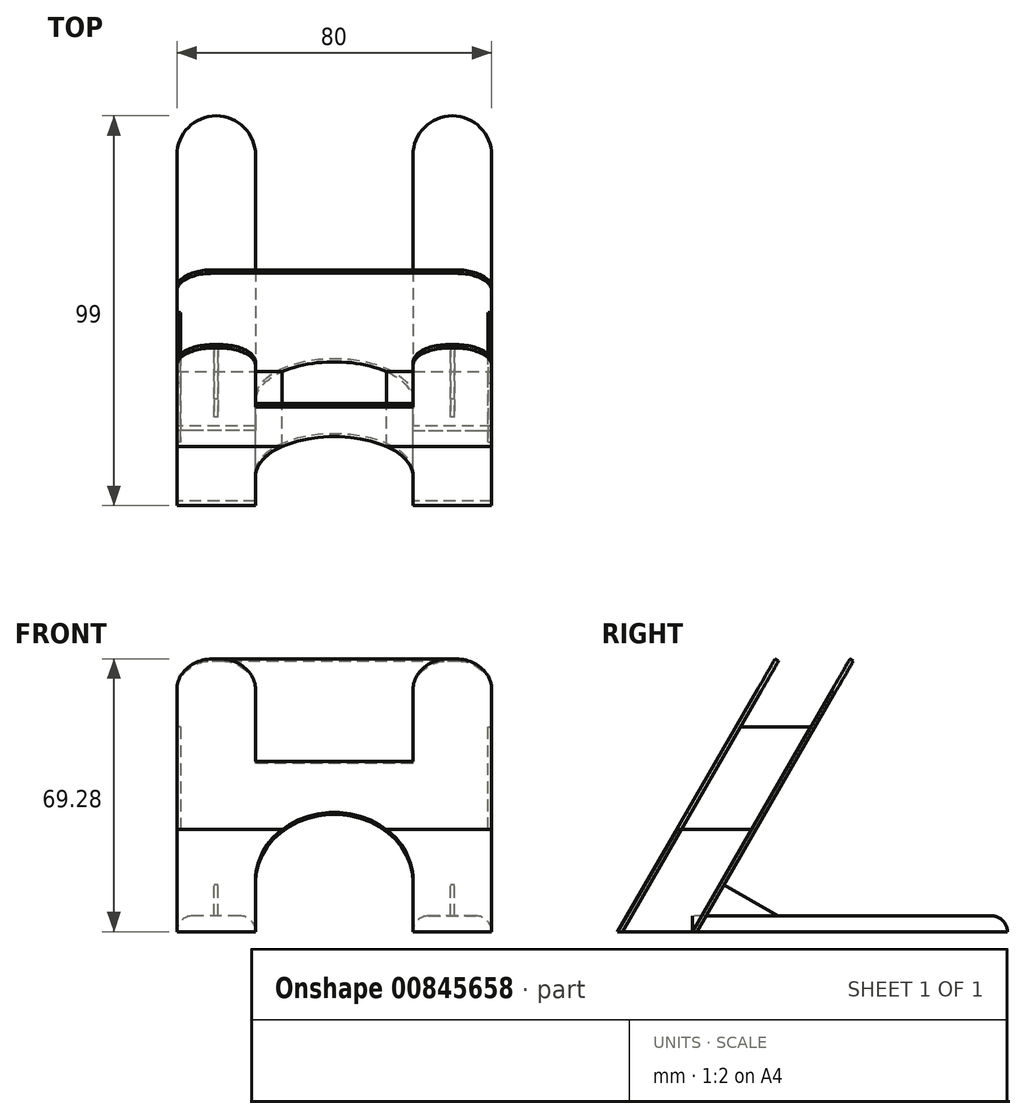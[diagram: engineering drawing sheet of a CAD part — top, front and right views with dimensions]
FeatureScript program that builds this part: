
annotation { "Feature Type Name" : "Feature", "Feature Type Description" : "" }
export const myFeature = defineFeature(function(context is Context, id is Id, definition is map)
    precondition{}
    {
        {
            var Q0;
            Q0=qCreatedBy(makeId("Top.planeOp"),FACE);
            var sketch = newSketch(context, id + "F0", { "sketchPlane" : qUnion([Q0])});
            skLineSegment(sketch, "E0.bottom", {"start": v(-30, 49.5) * mm, "end": v(-30, 49.5) * mm});
            skLineSegment(sketch, "E0.top", {"start": v(-40, -49.5) * mm, "end": v(40, -49.5) * mm});
            skLineSegment(sketch, "E0.left", {"start": v(-40, 39.5) * mm, "end": v(-40, -49.5) * mm});
            skLineSegment(sketch, "E0.right", {"start": v(40, 39.5) * mm, "end": v(40, -49.5) * mm});
            skPoint(sketch, "E0.middle", {"position": v(0, 0) * mm});
            skLineSegment(sketch, "E1.bottom", {"start": v(-20, 49.5) * mm, "end": v(-20, 49.5) * mm});
            skLineSegment(sketch, "E1.top", {"start": v(-20, -30.5) * mm, "end": v(20, -30.5) * mm});
            skLineSegment(sketch, "E1.left", {"start": v(-20, 39.5) * mm, "end": v(-20, -30.5) * mm});
            skLineSegment(sketch, "E1.right", {"start": v(20, 49.5) * mm, "end": v(20, 40) * mm});
            skLineSegment(sketch, "E2.bottom", {"start": v(20, -30.5) * mm, "end": v(-20, -30.5) * mm});
            skLineSegment(sketch, "E2.top", {"start": v(20, -49.5) * mm, "end": v(-20, -49.5) * mm});
            skLineSegment(sketch, "E2.left", {"start": v(20, -30.5) * mm, "end": v(20, -49.5) * mm});
            skLineSegment(sketch, "E2.right", {"start": v(-20, -30.5) * mm, "end": v(-20, -49.5) * mm});
            skLineSegment(sketch, "E3", {"start": v(-20, -30.5) * mm, "end": v(-40, -30.5) * mm});
            skLineSegment(sketch, "E4", {"start": v(20, -30.5) * mm, "end": v(40, -30.5) * mm});
            skLineSegment(sketch, "E5", {"start": v(20, 39.5) * mm, "end": v(20, -30.5) * mm});
            skLineSegment(sketch, "E6.trimOffspring", {"start": v(30, 49.5) * mm, "end": v(30, 49.5) * mm});
            skLineSegment(sketch, "E7", {"start": v(0, 54.54) * mm, "end": v(0, -63.88) * mm, "construction": true});
            skPoint(sketch, "E8.visualSharp", {"position": v(-40, 49.5) * mm});
            skArc(sketch, "E8.filletArc", {"start": v(-30, 49.5) * mm, "mid": v(-37.07, 46.57) * mm, "end": v(-40, 39.5) * mm});
            skPoint(sketch, "E9.visualSharp", {"position": v(-20, 49.5) * mm});
            skArc(sketch, "E9.filletArc", {"start": v(-20, 39.5) * mm, "mid": v(-22.93, 46.57) * mm, "end": v(-30, 49.5) * mm});
            skPoint(sketch, "E10.visualSharp", {"position": v(20, 49.5) * mm});
            skArc(sketch, "E10.filletArc", {"start": v(30, 49.5) * mm, "mid": v(22.93, 46.57) * mm, "end": v(20, 39.5) * mm});
            skPoint(sketch, "E11.visualSharp", {"position": v(40, 49.5) * mm});
            skArc(sketch, "E11.filletArc", {"start": v(40, 39.5) * mm, "mid": v(37.07, 46.57) * mm, "end": v(30, 49.5) * mm});
            skLineSegment(sketch, "E12", {"start": v(30, 49.5) * mm, "end": v(30, -55.74) * mm, "construction": true});
            skLineSegment(sketch, "E13", {"start": v(-30, 49.5) * mm, "end": v(-30, -57.66) * mm, "construction": true});
            skSolve(sketch);
        }
        {
            var Q0;
            Q0=sQuery(id+"F0.wireOp",EDGE,"E0.top");
            cPlane(context, id + "F1", {"entities" : qUnion([Q0]), "cplaneType" : CPlaneType.LINE_ANGLE, "offset" : 25 * mm, "angle" : 30 * degree, "oppositeDirection" : true, "width" : 150 * mm, "height" : 150 * mm});
        }
        {
            var Q0;
            Q0=sQuery(id+"F0.wireOp",EDGE,"E1.top");
            cPlane(context, id + "F2", {"entities" : qUnion([Q0]), "cplaneType" : CPlaneType.LINE_ANGLE, "offset" : 20 * mm, "angle" : 30 * degree, "oppositeDirection" : true, "width" : 150 * mm, "height" : 150 * mm});
        }
        {
            var Q0;
            Q0=qCreatedBy(id+"F2.planeOp",FACE);
            var sketch = newSketch(context, id + "F3", { "sketchPlane" : qUnion([Q0])});
            skLineSegment(sketch, "E14.bottom", {"start": v(40, -15.25) * mm, "end": v(-40, -15.25) * mm});
            skLineSegment(sketch, "E14.left", {"start": v(40, -15.25) * mm, "end": v(40, 64.75) * mm});
            skLineSegment(sketch, "E14.right", {"start": v(-40, -15.25) * mm, "end": v(-40, 64.75) * mm});
            skLineSegment(sketch, "E15.bottom", {"start": v(-20, -15.25) * mm, "end": v(20, -15.25) * mm});
            skLineSegment(sketch, "E15.top", {"start": v(0, 19.75) * mm, "end": v(0, 19.75) * mm});
            skLineSegment(sketch, "E15.left", {"start": v(-20, -15.25) * mm, "end": v(-20, -0.25) * mm});
            skLineSegment(sketch, "E15.right", {"start": v(20, -15.25) * mm, "end": v(20, -0.25) * mm});
            skPoint(sketch, "E16.visualSharp", {"position": v(-20, 19.75) * mm});
            skArc(sketch, "E16.filletArc", {"start": v(0, 19.75) * mm, "mid": v(-14.14, 13.9) * mm, "end": v(-20, -0.25) * mm});
            skPoint(sketch, "E17.visualSharp", {"position": v(20, 19.75) * mm});
            skArc(sketch, "E17.filletArc", {"start": v(20, -0.25) * mm, "mid": v(14.14, 13.9) * mm, "end": v(0, 19.75) * mm});
            skLineSegment(sketch, "E18", {"start": v(40, 14.75) * mm, "end": v(13.23, 14.75) * mm});
            skLineSegment(sketch, "E19", {"start": v(-13.23, 14.75) * mm, "end": v(-40, 14.75) * mm});
            skLineSegment(sketch, "E20", {"start": v(0, 99.97) * mm, "end": v(0, -38.35) * mm, "construction": true});
            skLineSegment(sketch, "E21.trimOffspring", {"start": v(40, 64.75) * mm, "end": v(-40, 64.75) * mm});
            skSolve(sketch);
        }
        {
            var Q0;
            Q0=qCreatedBy(id+"F1.planeOp",FACE);
            var sketch = newSketch(context, id + "F4", { "sketchPlane" : qUnion([Q0])});
            skLineSegment(sketch, "E22.bottom", {"start": v(40, -24.75) * mm, "end": v(-40, -24.75) * mm});
            skLineSegment(sketch, "E22.top", {"start": v(40, 55.25) * mm, "end": v(20, 55.25) * mm});
            skLineSegment(sketch, "E22.left", {"start": v(40, -24.75) * mm, "end": v(40, 55.25) * mm});
            skLineSegment(sketch, "E22.right", {"start": v(-40, -24.75) * mm, "end": v(-40, 55.25) * mm});
            skLineSegment(sketch, "E23.top", {"start": v(-20, 25.25) * mm, "end": v(20, 25.25) * mm});
            skLineSegment(sketch, "E23.left", {"start": v(-20, 55.25) * mm, "end": v(-20, 25.25) * mm});
            skLineSegment(sketch, "E23.right", {"start": v(20, 55.38) * mm, "end": v(20, 25.25) * mm});
            skLineSegment(sketch, "E24.bottom", {"start": v(-20, -24.75) * mm, "end": v(20, -24.75) * mm});
            skLineSegment(sketch, "E24.top", {"start": v(0, 10.25) * mm, "end": v(0, 10.25) * mm});
            skLineSegment(sketch, "E24.left", {"start": v(-20, -24.75) * mm, "end": v(-20, -9.75) * mm});
            skLineSegment(sketch, "E24.right", {"start": v(20, -24.75) * mm, "end": v(20, -9.75) * mm});
            skPoint(sketch, "E25.visualSharp", {"position": v(-20, 10.25) * mm});
            skArc(sketch, "E25.filletArc", {"start": v(0, 10.25) * mm, "mid": v(-14.14, 4.4) * mm, "end": v(-20, -9.75) * mm});
            skPoint(sketch, "E26.visualSharp", {"position": v(20, 10.25) * mm});
            skArc(sketch, "E26.filletArc", {"start": v(20, -9.75) * mm, "mid": v(14.14, 4.4) * mm, "end": v(0, 10.25) * mm});
            skLineSegment(sketch, "E27", {"start": v(40, 5.25) * mm, "end": v(13.23, 5.25) * mm});
            skLineSegment(sketch, "E28", {"start": v(-13.23, 5.25) * mm, "end": v(-40, 5.25) * mm});
            skLineSegment(sketch, "E29", {"start": v(0, 87.55) * mm, "end": v(0, -88.72) * mm, "construction": true});
            skLineSegment(sketch, "E30", {"start": v(20, 55.38) * mm, "end": v(20, 55.38) * mm});
            skLineSegment(sketch, "E31", {"start": v(-20, 55.25) * mm, "end": v(-40, 55.25) * mm});
            skSolve(sketch);
        }
        {
            var Q0;
            {var subQ2=sQuery(id+"F0.wireOp",EDGE,"E4");Q0=makeQuery(id+"F0.imprint","IMPRINT",FACE,{"disambiguationData":[TD([[makeQuery(id+"F0.imprint","IMPRINT",EDGE,{"derivedFrom":subQ2}),1.0]])]});}
            var Q1;
            Q1=makeQuery(id+"F0.imprint","IMPRINT",FACE,{"disambiguationData":[TD([[makeQuery(id+"F0.imprint","IMPRINT",EDGE,{"derivedFrom":sQuery(id+"F0.wireOp",EDGE,"E1.left")}),-1.0]])]});
            extrude(context, id + "F5", {"entities" : qUnion([Q0, Q1]), "depth" : 4 * mm, "offsetDistance" : 25 * mm});
        }
        {
            var Q0;
            {var subQ1=sQuery(id+"F4.wireOp",EDGE,"E24.left");Q0=makeQuery(id+"F4.imprint","IMPRINT",FACE,{"disambiguationData":[TD([[makeQuery(id+"F4.imprint","IMPRINT",EDGE,{"derivedFrom":subQ1}),1.0]])]});}
            var Q1;
            {var subQ6=sQuery(id+"F4.wireOp",EDGE,"E22.top");Q1=makeQuery(id+"F4.imprint","IMPRINT",FACE,{"disambiguationData":[TD([[makeQuery(id+"F4.imprint","IMPRINT",EDGE,{"derivedFrom":subQ6}),1.0]])]});}
            var Q2;
            {var subQ1=sQuery(id+"F4.wireOp",EDGE,"E24.right");Q2=makeQuery(id+"F4.imprint","IMPRINT",FACE,{"disambiguationData":[TD([[makeQuery(id+"F4.imprint","IMPRINT",EDGE,{"derivedFrom":subQ1}),-1.0]])]});}
            extrude(context, id + "F6", {"entities" : qUnion([Q0, Q1, Q2]), "depth" : 1 * mm, "offsetDistance" : 25 * mm});
        }
        {
            var Q0;
            {var subQ1=sQuery(id+"F3.wireOp",EDGE,"E15.left");Q0=makeQuery(id+"F3.imprint","IMPRINT",FACE,{"disambiguationData":[TD([[makeQuery(id+"F3.imprint","IMPRINT",EDGE,{"derivedFrom":subQ1}),1.0]])]});}
            var Q1;
            {var subQ5=sQuery(id+"F3.wireOp",EDGE,"E14.top");Q1=makeQuery(id+"F3.imprint","IMPRINT",FACE,{"disambiguationData":[TD([[makeQuery(id+"F3.imprint","IMPRINT",EDGE,{"derivedFrom":subQ5}),1.0]])]});}
            var Q2;
            {var subQ1=sQuery(id+"F3.wireOp",EDGE,"E15.right");Q2=makeQuery(id+"F3.imprint","IMPRINT",FACE,{"disambiguationData":[TD([[makeQuery(id+"F3.imprint","IMPRINT",EDGE,{"derivedFrom":subQ1}),-1.0]])]});}
            var Q3;
            {var subQ3=sQuery(id+"F3.wireOp",EDGE,"E18");Q3=makeQuery(id+"F3.imprint","IMPRINT",FACE,{"disambiguationData":[TD([[makeQuery(id+"F3.imprint","IMPRINT",EDGE,{"derivedFrom":subQ3}),-1.0]])]});}
            extrude(context, id + "F7", {"entities" : qUnion([Q0, Q1, Q2, Q3]), "depth" : 1 * mm, "offsetDistance" : 25 * mm});
        }
        {
            var Q0;
            {var subQ1=sQuery(id+"F4.wireOp",EDGE,"E24.left");Q0=makeQuery(id+"F4.imprint","IMPRINT",FACE,{"disambiguationData":[TD([[makeQuery(id+"F4.imprint","IMPRINT",EDGE,{"derivedFrom":subQ1}),1.0]])]});}
            var Q1;
            {var subQ1=sQuery(id+"F3.wireOp",EDGE,"E15.left");Q1=makeQuery(id+"F3.imprint","IMPRINT",FACE,{"disambiguationData":[TD([[makeQuery(id+"F3.imprint","IMPRINT",EDGE,{"derivedFrom":subQ1}),1.0]])]});}
            loft(context, id + "F8", {"sheetProfilesArray" : [{ "sheetProfileEntities" : qUnion([Q0]) }, { "sheetProfileEntities" : qUnion([Q1]) }]});
        }
        {
            var Q0;
            {var subQ1=sQuery(id+"F4.wireOp",EDGE,"E24.right");Q0=makeQuery(id+"F4.imprint","IMPRINT",FACE,{"disambiguationData":[TD([[makeQuery(id+"F4.imprint","IMPRINT",EDGE,{"derivedFrom":subQ1}),-1.0]])]});}
            var Q1;
            {var subQ1=sQuery(id+"F3.wireOp",EDGE,"E15.right");Q1=makeQuery(id+"F3.imprint","IMPRINT",FACE,{"disambiguationData":[TD([[makeQuery(id+"F3.imprint","IMPRINT",EDGE,{"derivedFrom":subQ1}),-1.0]])]});}
            loft(context, id + "F9", {"sheetProfilesArray" : [{ "sheetProfileEntities" : qUnion([Q0]) }, { "sheetProfileEntities" : qUnion([Q1]) }]});
        }
        {
            var Q0;
            Q0=makeQuery(id+"F6.opExtrude","SWEPT_EDGE",EDGE,{"disambiguationData":[OSD([sQuery(id+"F4.wireOp",EDGE,"E22.top"),sQuery(id+"F4.wireOp",EDGE,"E22.left")])]});
            var Q1;
            Q1=makeQuery(id+"F6.opExtrude","SWEPT_EDGE",EDGE,{"disambiguationData":[OSD([sQuery(id+"F4.wireOp",EDGE,"E22.top"),sQuery(id+"F4.wireOp",EDGE,"E23.right")])]});
            var Q2;
            Q2=makeQuery(id+"F7.opExtrude","SWEPT_EDGE",EDGE,{"disambiguationData":[OSD([sQuery(id+"F3.wireOp",EDGE,"E14.top"),sQuery(id+"F3.wireOp",EDGE,"af3756bd-d7f4-4d2d-9217-8fff7642af17.right")])]});
            var Q3;
            {var subQ0=sQuery(id+"F3.wireOp",EDGE,"E21.trimOffspring");Q3=qUnion([makeQuery(id+"F7.opExtrude","SWEPT_EDGE",EDGE,{"disambiguationData":[OSD([sQuery(id+"F3.wireOp",EDGE,"E14.right"),subQ0])]}),makeQuery(id+"F7.opExtrude","SWEPT_EDGE",EDGE,{"disambiguationData":[OSD([sQuery(id+"F3.wireOp",EDGE,"E14.left"),subQ0])]})]);}
            var Q4;
            Q4=makeQuery(id+"F7.opExtrude","SWEPT_EDGE",EDGE,{"disambiguationData":[OSD([sQuery(id+"F3.wireOp",EDGE,"E14.right"),sQuery(id+"F3.wireOp",EDGE,"E21.trimOffspring")])]});
            var Q5;
            Q5=makeQuery(id+"F6.opExtrude","SWEPT_EDGE",EDGE,{"disambiguationData":[OSD([sQuery(id+"F4.wireOp",EDGE,"E22.right"),sQuery(id+"F4.wireOp",EDGE,"E31")])]});
            var Q6;
            Q6=makeQuery(id+"F6.opExtrude","SWEPT_EDGE",EDGE,{"disambiguationData":[OSD([sQuery(id+"F4.wireOp",EDGE,"E23.left"),sQuery(id+"F4.wireOp",EDGE,"E31")])]});
            fillet(context, id + "F10", {"entities" : qUnion([Q0, Q1, Q2, Q3, Q4, Q5, Q6]), "radius" : 9 * mm, "tangentPropagation" : true, "allowEdgeOverflow" : false});
        }
        {
            var Q0;
            Q0=makeQuery(id+"F5.opExtrude","CAP_EDGE",EDGE,{"disambiguationData":[OSD([sQuery(id+"F0.wireOp",EDGE,"E0.left")])],"isStart":false});
            var Q1;
            Q1=makeQuery(id+"F5.opExtrude","CAP_EDGE",EDGE,{"disambiguationData":[OSD([sQuery(id+"F0.wireOp",EDGE,"E1.left")])],"isStart":false});
            var Q2;
            Q2=makeQuery(id+"F5.opExtrude","CAP_EDGE",EDGE,{"disambiguationData":[OSD([sQuery(id+"F0.wireOp",EDGE,"E5")])],"isStart":false});
            var Q3;
            Q3=makeQuery(id+"F5.opExtrude","CAP_EDGE",EDGE,{"disambiguationData":[OSD([sQuery(id+"F0.wireOp",EDGE,"E0.right")])],"isStart":false});
            var Q4;
            Q4=makeQuery(id+"F5.opExtrude","CAP_EDGE",EDGE,{"disambiguationData":[OSD([sQuery(id+"F0.wireOp",EDGE,"E10.filletArc"),sQuery(id+"F0.wireOp",EDGE,"E11.filletArc")])],"isStart":false});
            var Q5;
            Q5=makeQuery(id+"F5.opExtrude","CAP_EDGE",EDGE,{"disambiguationData":[OSD([sQuery(id+"F0.wireOp",EDGE,"E8.filletArc"),sQuery(id+"F0.wireOp",EDGE,"E9.filletArc")])],"isStart":false});
            fillet(context, id + "F11", {"entities" : qUnion([Q0, Q1, Q2, Q3, Q4, Q5]), "radius" : 4 * mm, "tangentPropagation" : true, "allowEdgeOverflow" : false});
        }
        {
            var Q0;
            Q0=makeQuery(id+"F9.opLoft","SWEPT_FACE",FACE,{"disambiguationData":[OSD([sQuery(id+"F3.wireOp",EDGE,"E14.bottom"),sQuery(id+"F3.wireOp",EDGE,"E14.left"),sQuery(id+"F3.wireOp",EDGE,"E18"),sQuery(id+"F4.wireOp",EDGE,"E22.bottom"),sQuery(id+"F4.wireOp",EDGE,"E22.left"),sQuery(id+"F4.wireOp",EDGE,"E27")])]});
            cPlane(context, id + "F12", {"entities" : qUnion([Q0]), "cplaneType" : CPlaneType.OFFSET, "offset" : 0 * mm, "width" : 150 * mm, "height" : 150 * mm});
        }
        {
            var Q0;
            Q0=makeQuery(id+"F8.opLoft","SWEPT_FACE",FACE,{"disambiguationData":[OSD([sQuery(id+"F3.wireOp",EDGE,"E14.bottom"),sQuery(id+"F3.wireOp",EDGE,"E14.right"),sQuery(id+"F3.wireOp",EDGE,"E19"),sQuery(id+"F4.wireOp",EDGE,"E22.bottom"),sQuery(id+"F4.wireOp",EDGE,"E22.right"),sQuery(id+"F4.wireOp",EDGE,"E28")])]});
            cPlane(context, id + "F13", {"entities" : qUnion([Q0]), "cplaneType" : CPlaneType.OFFSET, "offset" : 0 * mm, "width" : 150 * mm, "height" : 150 * mm});
        }
        {
            var Q0;
            Q0=qCreatedBy(id+"F12.planeOp",FACE);
            var sketch = newSketch(context, id + "F14", { "sketchPlane" : qUnion([Q0])});
            skLineSegment(sketch, "E32", {"start": v(33.35, 25.98) * mm, "end": v(15.5, 25.98) * mm});
            skLineSegment(sketch, "E33", {"start": v(15.5, 25.98) * mm, "end": v(0.5, 51.96) * mm});
            skLineSegment(sketch, "E34", {"start": v(0.5, 51.96) * mm, "end": v(18.35, 51.96) * mm});
            skLineSegment(sketch, "E35", {"start": v(18.35, 51.96) * mm, "end": v(33.35, 25.98) * mm});
            skSolve(sketch);
        }
        {
            var Q0;
            Q0=makeQuery(id+"F14.imprint","IMPRINT",FACE,{"disambiguationData":[TD([[makeQuery(id+"F14.imprint","IMPRINT",EDGE,{"derivedFrom":sQuery(id+"F14.wireOp",EDGE,"E32")}),-1.0]])]});
            extrude(context, id + "F15", {"entities" : qUnion([Q0]), "oppositeDirection" : true, "depth" : 1 * mm, "offsetDistance" : 25 * mm});
        }
        {
            var Q0;
            Q0=qCreatedBy(id+"F13.planeOp",FACE);
            var sketch = newSketch(context, id + "F16", { "sketchPlane" : qUnion([Q0])});
            skLineSegment(sketch, "E36", {"start": v(-33.35, 25.98) * mm, "end": v(-18.35, 51.96) * mm});
            skLineSegment(sketch, "E37", {"start": v(-18.35, 51.96) * mm, "end": v(-0.5, 51.96) * mm});
            skLineSegment(sketch, "E38", {"start": v(-0.5, 51.96) * mm, "end": v(-15.5, 25.98) * mm});
            skLineSegment(sketch, "E39", {"start": v(-15.5, 25.98) * mm, "end": v(-33.35, 25.98) * mm});
            skSolve(sketch);
        }
        {
            var Q0;
            Q0=makeQuery(id+"F16.imprint","IMPRINT",FACE,{"disambiguationData":[TD([[makeQuery(id+"F16.imprint","IMPRINT",EDGE,{"derivedFrom":sQuery(id+"F16.wireOp",EDGE,"E36")}),-1.0]])]});
            extrude(context, id + "F17", {"entities" : qUnion([Q0]), "oppositeDirection" : true, "depth" : 1 * mm, "offsetDistance" : 25 * mm});
        }
        {
            var Q0;
            Q0=sQuery(id+"F0.wireOp",EDGE,"E12");
            cPlane(context, id + "F18", {"entities" : qUnion([Q0]), "cplaneType" : CPlaneType.LINE_ANGLE, "offset" : 25 * mm, "angle" : 90 * degree, "width" : 150 * mm, "height" : 150 * mm});
        }
        {
            var Q0;
            Q0=qCreatedBy(id+"F18.planeOp",FACE);
            var sketch = newSketch(context, id + "F19", { "sketchPlane" : qUnion([Q0])});
            skLineSegment(sketch, "E40", {"start": v(-27.04, 4) * mm, "end": v(-22.46, 11.93) * mm});
            skLineSegment(sketch, "E41", {"start": v(-22.46, 11.93) * mm, "end": v(-8.73, 4) * mm});
            skLineSegment(sketch, "E42", {"start": v(-8.73, 4) * mm, "end": v(-27.04, 4) * mm});
            skSolve(sketch);
        }
        {
            var Q0;
            Q0=makeQuery(id+"F19.imprint","IMPRINT",FACE,{"disambiguationData":[TD([[makeQuery(id+"F19.imprint","IMPRINT",EDGE,{"derivedFrom":sQuery(id+"F19.wireOp",EDGE,"E40")}),-1.0]])]});
            extrude(context, id + "F20", {"entities" : qUnion([Q0]), "endBound" : BoundingType.SYMMETRIC, "depth" : 1 * mm, "offsetDistance" : 25 * mm});
        }
        {
            var Q0;
            {var subQ0=sQuery(id+"F3.wireOp",EDGE,"E14.bottom");Q0=makeQuery(id+"F7.opExtrude","CAP_EDGE",EDGE,{"disambiguationData":[OSD([subQ0]),TDD([makeQuery(id+"F3.imprint","IMPRINT",EDGE,{"disambiguationData":[TD([[makeQuery(id+"F3.imprint","INTERSECT",VERTEX,{"derivedFrom":[subQ0,sQuery(id+"F3.wireOp",EDGE,"E15.left")]}),-1.0]])],"derivedFrom":subQ0})])],"isStart":false});}
            chamfer(context, id + "F21", {"entities" : qUnion([Q0]), "chamferType" : ChamferType.OFFSET_ANGLE, "width" : 1 * mm, "oppositeDirection" : false, "angle" : 30 * degree, "tangentPropagation" : true});
        }
        {
            var Q0;
            {var subQ0=sQuery(id+"F3.wireOp",EDGE,"E14.bottom");Q0=makeQuery(id+"F7.opExtrude","CAP_EDGE",EDGE,{"disambiguationData":[OSD([subQ0]),TDD([makeQuery(id+"F3.imprint","IMPRINT",EDGE,{"disambiguationData":[TD([[makeQuery(id+"F3.imprint","INTERSECT",VERTEX,{"derivedFrom":[subQ0,sQuery(id+"F3.wireOp",EDGE,"E15.right")]}),1.0]])],"derivedFrom":subQ0})])],"isStart":false});}
            var Q1;
            {var subQ0=sQuery(id+"F4.wireOp",EDGE,"E22.bottom");Q1=makeQuery(id+"F6.opExtrude","CAP_EDGE",EDGE,{"disambiguationData":[OSD([subQ0]),TDD([makeQuery(id+"F4.imprint","IMPRINT",EDGE,{"disambiguationData":[TD([[makeQuery(id+"F4.imprint","INTERSECT",VERTEX,{"derivedFrom":[subQ0,sQuery(id+"F4.wireOp",EDGE,"E24.left")]}),-1.0]])],"derivedFrom":subQ0})])],"isStart":false});}
            var Q2;
            {var subQ0=sQuery(id+"F4.wireOp",EDGE,"E22.bottom");Q2=makeQuery(id+"F6.opExtrude","CAP_EDGE",EDGE,{"disambiguationData":[OSD([subQ0]),TDD([makeQuery(id+"F4.imprint","IMPRINT",EDGE,{"disambiguationData":[TD([[makeQuery(id+"F4.imprint","INTERSECT",VERTEX,{"derivedFrom":[subQ0,sQuery(id+"F4.wireOp",EDGE,"E24.right")]}),1.0]])],"derivedFrom":subQ0})])],"isStart":false});}
            chamfer(context, id + "F22", {"entities" : qUnion([Q0, Q1, Q2]), "chamferType" : ChamferType.OFFSET_ANGLE, "width" : 1 * mm, "oppositeDirection" : false, "angle" : 30 * degree, "tangentPropagation" : true});
        }
        {
            var Q0;
            Q0=sQuery(id+"F0.wireOp",EDGE,"E13");
            cPlane(context, id + "F23", {"entities" : qUnion([Q0]), "cplaneType" : CPlaneType.LINE_ANGLE, "offset" : 25 * mm, "angle" : 90 * degree, "width" : 150 * mm, "height" : 150 * mm});
        }
        {
            var Q0;
            Q0=qCreatedBy(id+"F23.planeOp",FACE);
            var sketch = newSketch(context, id + "F24", { "sketchPlane" : qUnion([Q0])});
            skLineSegment(sketch, "E43", {"start": v(-27.04, 4) * mm, "end": v(-22.49, 11.88) * mm});
            skLineSegment(sketch, "E44", {"start": v(-22.49, 11.88) * mm, "end": v(-8.84, 4) * mm});
            skLineSegment(sketch, "E45", {"start": v(-8.84, 4) * mm, "end": v(-27.04, 4) * mm});
            skSolve(sketch);
        }
        {
            var Q0;
            Q0=makeQuery(id+"F24.imprint","IMPRINT",FACE,{"disambiguationData":[TD([[makeQuery(id+"F24.imprint","IMPRINT",EDGE,{"derivedFrom":sQuery(id+"F24.wireOp",EDGE,"E43")}),-1.0]])]});
            extrude(context, id + "F25", {"entities" : qUnion([Q0]), "endBound" : BoundingType.SYMMETRIC, "depth" : 1 * mm, "offsetDistance" : 25 * mm});
        }
    });
